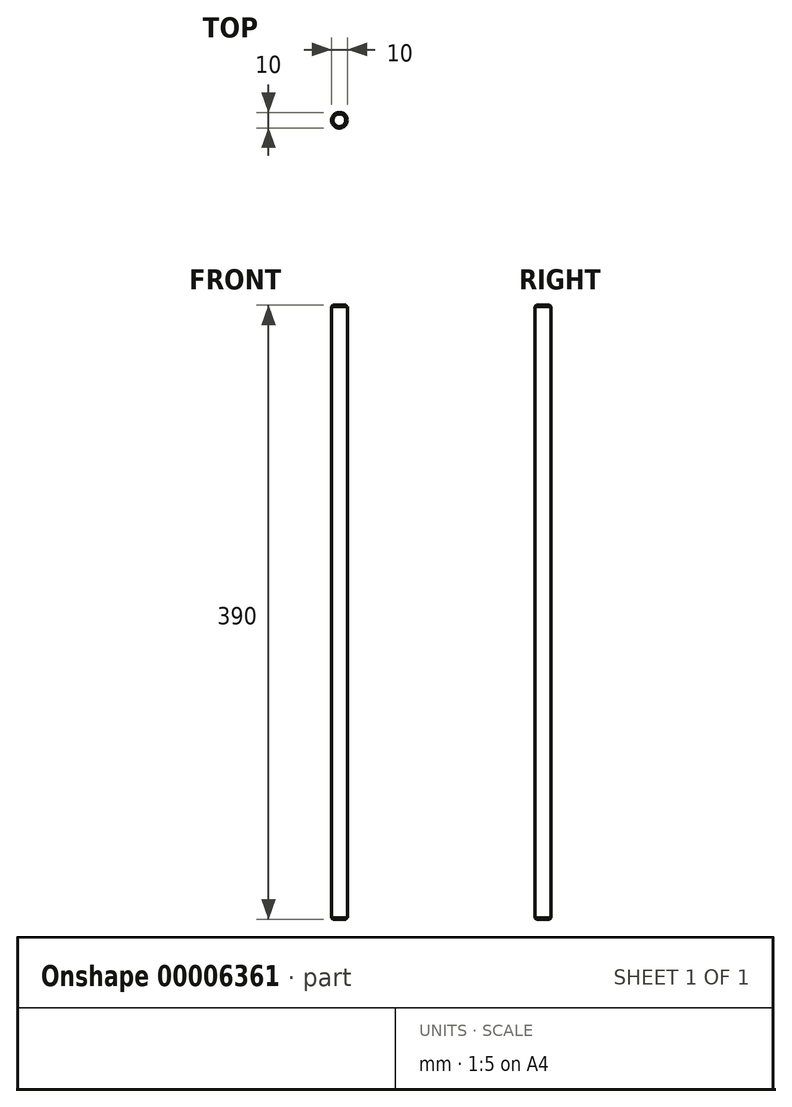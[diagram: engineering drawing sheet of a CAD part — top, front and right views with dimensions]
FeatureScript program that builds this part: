
annotation { "Feature Type Name" : "Feature", "Feature Type Description" : "" }
export const myFeature = defineFeature(function(context is Context, id is Id, definition is map)
    precondition{}
    {
        {
            var Q0;
            Q0=qCreatedBy(makeId("Top.planeOp"),FACE);
            var sketch = newSketch(context, id + "F0", { "sketchPlane" : qUnion([Q0])});
            skCircle(sketch, "E0", {"center": v(0, 0) * mm, "radius": 5 * mm});
            skSolve(sketch);
        }
        {
            var Q0;
            Q0=makeQuery(id+"F0.imprint","IMPRINT",FACE,{"disambiguationData":[TD([[makeQuery(id+"F0.imprint","IMPRINT",EDGE,{"derivedFrom":sQuery(id+"F0.wireOp",EDGE,"E0")}),1.0]])]});
            extrude(context, id + "F1", {"entities" : qUnion([Q0]), "oppositeDirection" : true, "depth" : 390 * mm});
        }
        {
            var Q0;
            Q0=makeQuery(id+"F1.opExtrude","CAP_EDGE",EDGE,{"disambiguationData":[OSD([sQuery(id+"F0.wireOp",EDGE,"E0")])],"isStart":true});
            chamfer(context, id + "F2", {"entities" : qUnion([Q0]), "width" : 1 * mm, "tangentPropagation" : true});
        }
        {
            var Q0;
            Q0=makeQuery(id+"F1.opExtrude","CAP_EDGE",EDGE,{"disambiguationData":[OSD([sQuery(id+"F0.wireOp",EDGE,"E0")])],"isStart":false});
            chamfer(context, id + "F3", {"entities" : qUnion([Q0]), "width" : 1 * mm, "tangentPropagation" : true});
        }
    });
